# Revit family: Dynamic Fenestration - Awning Out Swing Cam
name_source: partatom
category: Windows
units: mm (PartAtom-declared; Revit-internal decimal feet)

## family parameters
Always vertical = Yes
Cut with Voids When Loaded = No
Host = Wall
OmniClass Number = 23.30.20.00
OmniClass Title = Windows
Room Calculation Point = No
Shared = No

## types (1)
- Dynamic Fenestration - Awning Out Swing Cam
    Analytic Construction = <None>
    Default Sill Height = 36"
    Define Thermal Properties by = Schematic Type
    Description = Awning Out Swing Cam
    Frame Material = Arte Metal
    Gap Fill = Argon
    Glass Material = Glass
    Glass Type = Triple Silve LowE / Clear
    Height = 48"
    Manufacturer = Dynamic Fenestration
    Max. Height = 130"
    Max. Width = 94"
    Min. Height = 14"
    Min. Width = 12"
    Model = Awning Out Swing
    Rough Height = 50"
    Rough Width = 38"
    Type Comments = H Profile
    Wall Closure = By host
    Width = 36"

## geometry (parser evidence)
native form markers: Sweep x8
no freeform markers — native parametric forms only
